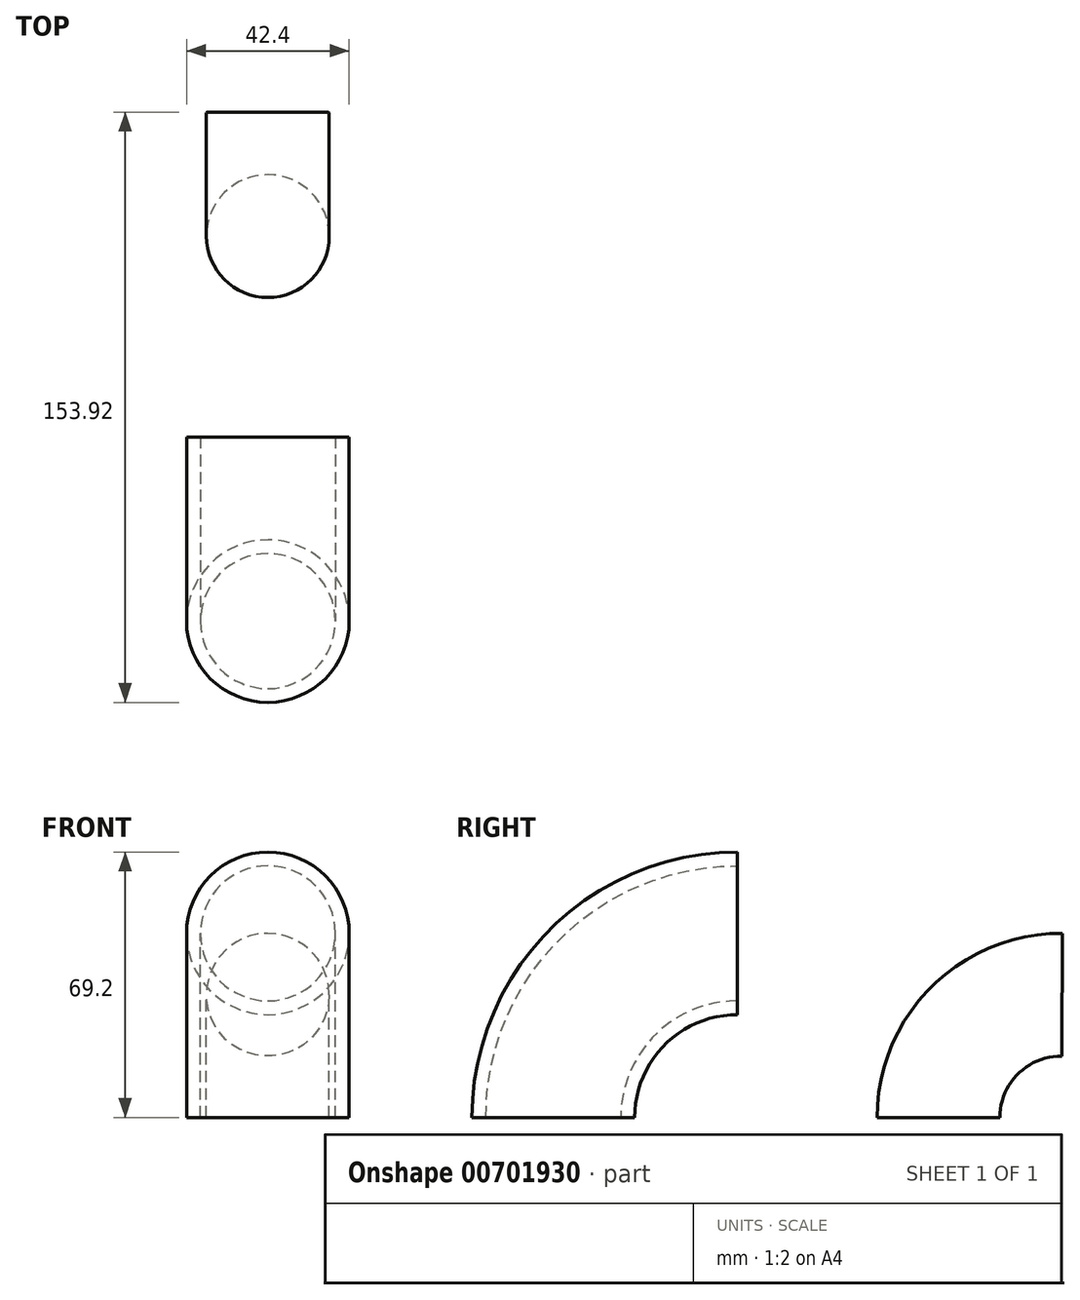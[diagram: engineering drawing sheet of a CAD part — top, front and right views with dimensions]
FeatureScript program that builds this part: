
annotation { "Feature Type Name" : "Feature", "Feature Type Description" : "" }
export const myFeature = defineFeature(function(context is Context, id is Id, definition is map)
    precondition{}
    {
        {
            var Q0;
            Q0=qCreatedBy(makeId("Top.planeOp"),FACE);
            var sketch = newSketch(context, id + "F0", { "sketchPlane" : qUnion([Q0])});
            skCircle(sketch, "E0", {"center": v(0, 0) * mm, "radius": 21.2 * mm});
            skSolve(sketch);
        }
        {
            var Q0;
            Q0=qCreatedBy(makeId("Right.planeOp"),FACE);
            var sketch = newSketch(context, id + "F1", { "sketchPlane" : qUnion([Q0])});
            skLineSegment(sketch, "E1", {"start": v(0, 0) * mm, "end": v(0, 0) * mm});
            skLineSegment(sketch, "E2", {"start": v(48, 48) * mm, "end": v(48, 48) * mm});
            skPoint(sketch, "E3.visualSharp", {"position": v(0, 48) * mm});
            skArc(sketch, "E3.filletArc", {"start": v(48, 48) * mm, "mid": v(14.06, 33.94) * mm, "end": v(0, 0) * mm});
            skSolve(sketch);
        }
        {
            var Q0;
            Q0=qCreatedBy(makeId("Top.planeOp"),FACE);
            var sketch = newSketch(context, id + "F2", { "sketchPlane" : qUnion([Q0])});
            skCircle(sketch, "E4", {"center": v(0, 100.4) * mm, "radius": 16 * mm});
            skSolve(sketch);
        }
        {
            var Q0;
            Q0=qCreatedBy(makeId("Right.planeOp"),FACE);
            var sketch = newSketch(context, id + "F3", { "sketchPlane" : qUnion([Q0])});
            skArc(sketch, "E5", {"start": v(100.4, 0) * mm, "mid": v(109.84, 22.7) * mm, "end": v(132.61, 32) * mm});
            skSolve(sketch);
        }
        {
            var Q0;
            Q0=makeQuery(id+"F2.imprint","IMPRINT",FACE,{"disambiguationData":[TD([[makeQuery(id+"F2.imprint","IMPRINT",EDGE,{"derivedFrom":sQuery(id+"F2.wireOp",EDGE,"E4")}),1.0]])]});
            var Q1;
            Q1=sQuery(id+"F3.wireOp",EDGE,"E5");
            sweep(context, id + "F4", {"profiles" : qUnion([Q0]), "path" : qUnion([Q1])});
        }
        {
            var Q0;
            Q0 = qSketchRegion(id + "F0", true);
            var Q1;
            Q1 = qConstructionFilter(qBodyType(qCreatedBy(id + "F1" ,EDGE), BodyType.WIRE), ConstructionObject.NO);
            sweep(context, id + "F5", {"profiles" : qUnion([Q0]), "path" : qUnion([Q1])});
        }
        {
            var Q0;
            Q0=makeQuery(id+"F5.opSweep","CAP_FACE",FACE,{"disambiguationData":[OSD([sQuery(id+"F0.wireOp",EDGE,"E0"),sQuery(id+"F1.wireOp",VERTEX,"E3.filletArc.start")])],"isStart":false});
            var Q1;
            Q1=makeQuery(id+"F5.opSweep","CAP_FACE",FACE,{"disambiguationData":[OSD([sQuery(id+"F0.wireOp",EDGE,"E0"),sQuery(id+"F1.wireOp",VERTEX,"E3.filletArc.end")])],"isStart":true});
            shell(context, id + "F6", {"entities" : qUnion([Q0, Q1]), "thickness" : 3.6 * mm});
        }
    });
